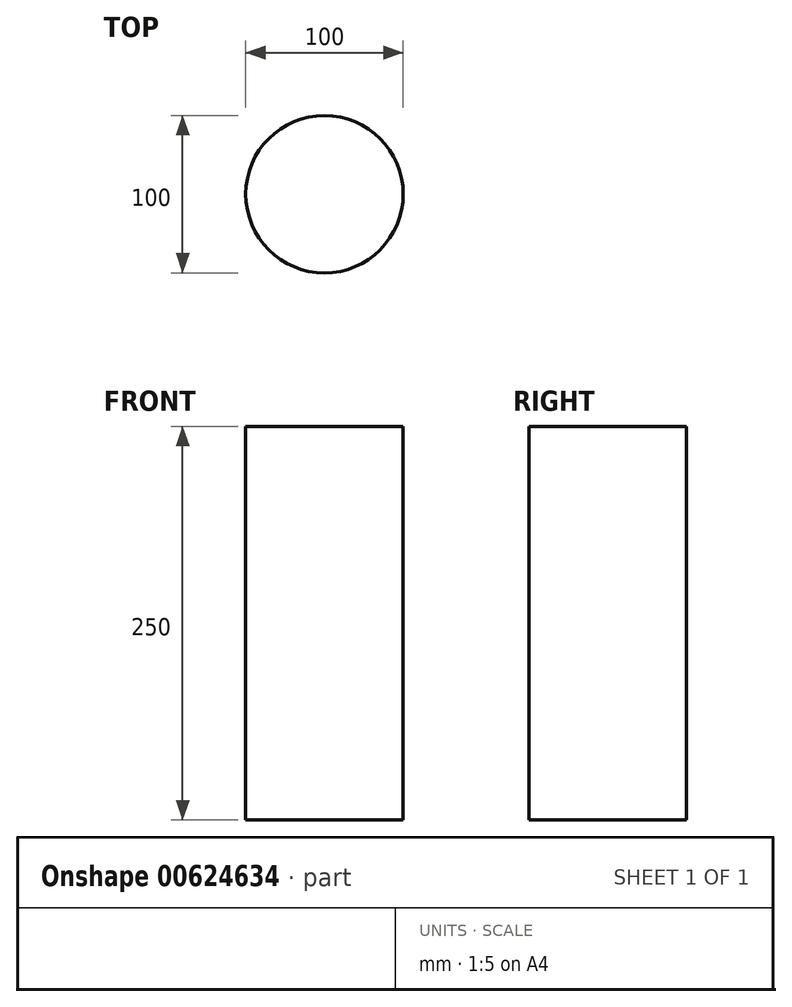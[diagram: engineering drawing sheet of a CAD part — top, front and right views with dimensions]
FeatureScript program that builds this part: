
annotation { "Feature Type Name" : "Feature", "Feature Type Description" : "" }
export const myFeature = defineFeature(function(context is Context, id is Id, definition is map)
    precondition{}
    {
        {
            var Q0;
            Q0=qCreatedBy(makeId("Top.planeOp"),FACE);
            var sketch = newSketch(context, id + "F0", { "sketchPlane" : qUnion([Q0])});
            skCircle(sketch, "E0", {"center": v(0, 0) * mm, "radius": 50 * mm});
            skSolve(sketch);
        }
        {
            var Q0;
            Q0=makeQuery(id+"F0.imprint","IMPRINT",FACE,{"disambiguationData":[TD([[makeQuery(id+"F0.imprint","IMPRINT",EDGE,{"derivedFrom":sQuery(id+"F0.wireOp",EDGE,"E0")}),1.0]])]});
            extrude(context, id + "F1", {"entities" : qUnion([Q0]), "depth" : 250 * mm, "offsetDistance" : 25 * mm});
        }
    });
